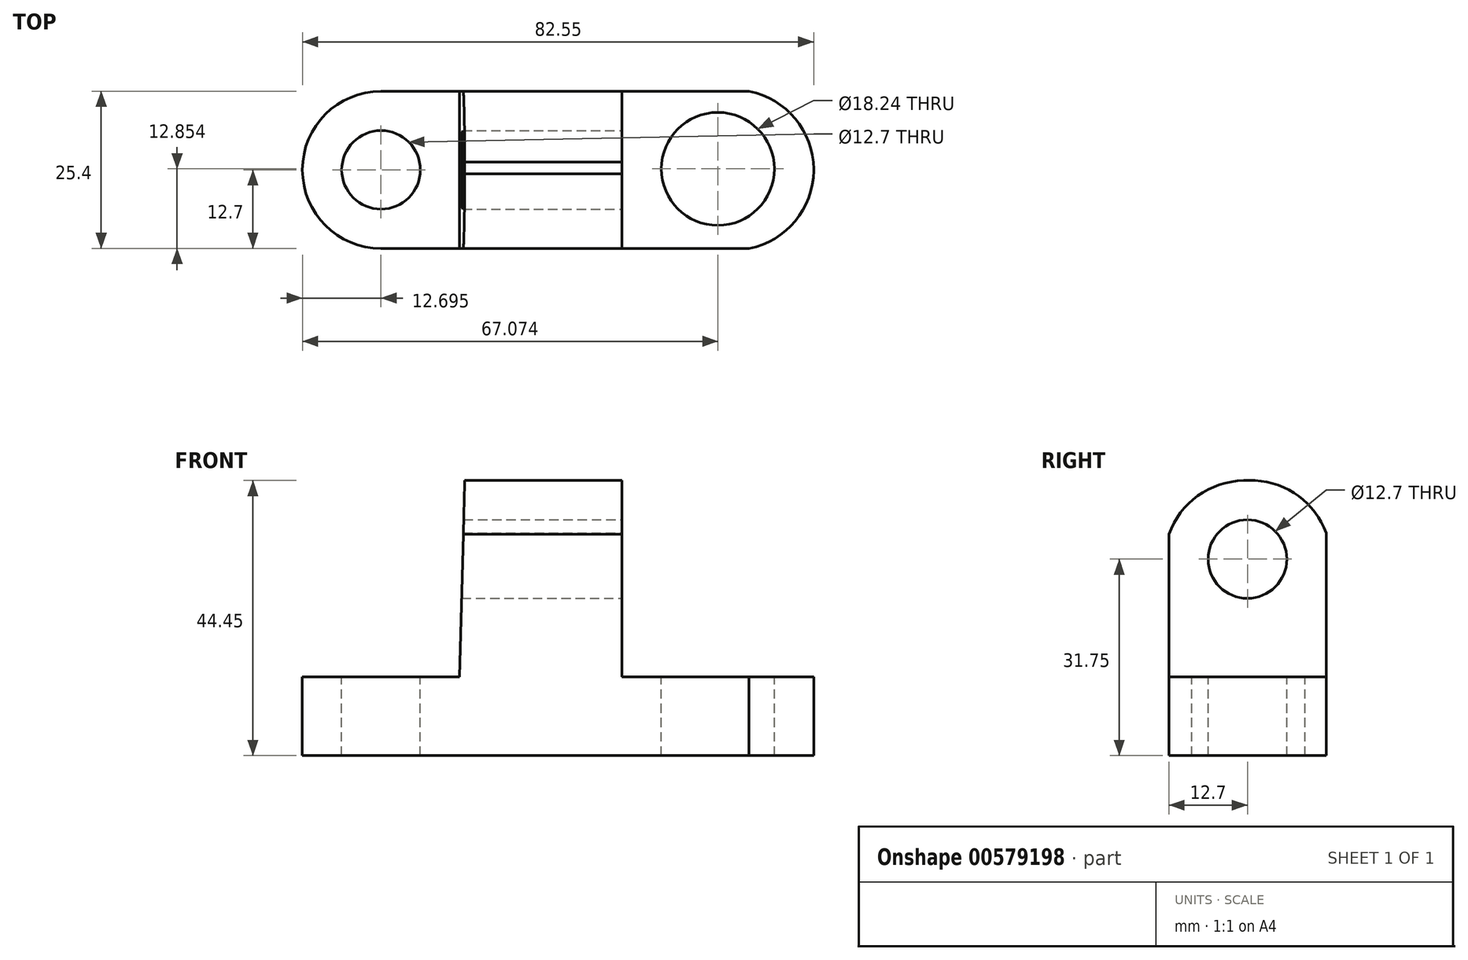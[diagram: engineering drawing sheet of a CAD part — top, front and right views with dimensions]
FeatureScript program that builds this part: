
annotation { "Feature Type Name" : "Feature", "Feature Type Description" : "" }
export const myFeature = defineFeature(function(context is Context, id is Id, definition is map)
    precondition{}
    {
        {
            var Q0;
            Q0=qCreatedBy(makeId("Front.planeOp"),FACE);
            var sketch = newSketch(context, id + "F0", { "sketchPlane" : qUnion([Q0])});
            skLineSegment(sketch, "E0", {"start": v(-96.25, 12.7) * mm, "end": v(-96.25, 0) * mm});
            skLineSegment(sketch, "E1", {"start": v(-96.25, 0) * mm, "end": v(-13.7, 0) * mm});
            skLineSegment(sketch, "E2", {"start": v(-13.7, 0) * mm, "end": v(-13.7, 12.7) * mm});
            skLineSegment(sketch, "E3", {"start": v(-13.7, 12.7) * mm, "end": v(-44.65, 12.7) * mm});
            skLineSegment(sketch, "E4", {"start": v(-44.65, 12.7) * mm, "end": v(-44.65, 44.45) * mm});
            skLineSegment(sketch, "E5", {"start": v(-44.65, 44.45) * mm, "end": v(-70.05, 44.45) * mm});
            skLineSegment(sketch, "E6", {"start": v(-96.25, 12.7) * mm, "end": v(-70.85, 12.7) * mm});
            skLineSegment(sketch, "E7", {"start": v(-70.85, 12.7) * mm, "end": v(-70.05, 44.45) * mm});
            skSolve(sketch);
        }
        {
            var Q0;
            Q0=makeQuery(id+"F0.imprint","IMPRINT",FACE,{"disambiguationData":[TD([[makeQuery(id+"F0.imprint","IMPRINT",EDGE,{"derivedFrom":sQuery(id+"F0.wireOp",EDGE,"E0")}),1.0]])]});
            extrude(context, id + "F1", {"entities" : qUnion([Q0]), "depth" : 25.4 * mm, "offsetDistance" : 25.4 * mm});
        }
        {
            var Q0;
            Q0=makeQuery(id+"F1.opExtrude","SWEPT_FACE",FACE,{"disambiguationData":[OSD([sQuery(id+"F0.wireOp",EDGE,"E4")])]});
            var sketch = newSketch(context, id + "F2", { "sketchPlane" : qUnion([Q0])});
            skCircle(sketch, "E8", {"center": v(-12.7, 31.75) * mm, "radius": 6.35 * mm});
            skSolve(sketch);
        }
        {
            var Q0;
            Q0=makeQuery(id+"F2.imprint","IMPRINT",FACE,{"disambiguationData":[TD([[makeQuery(id+"F2.imprint","IMPRINT",EDGE,{"derivedFrom":sQuery(id+"F2.wireOp",EDGE,"E8")}),1.0]])]});
            extrude(context, id + "F3", {"entities" : qUnion([Q0]), "operationType" : NewBodyOperationType.REMOVE, "endBound" : BoundingType.THROUGH_ALL, "oppositeDirection" : true, "depth" : 25.4 * mm, "offsetDistance" : 25.4 * mm});
        }
        {
            var Q0;
            Q0=makeQuery(id+"F1.opExtrude","SWEPT_FACE",FACE,{"disambiguationData":[OSD([sQuery(id+"F0.wireOp",EDGE,"E4")])]});
            var sketch = newSketch(context, id + "F4", { "sketchPlane" : qUnion([Q0])});
            skArc(sketch, "E9", {"start": v(-12.7, 44.45) * mm, "mid": v(-20.45, 42.15) * mm, "end": v(-25.4, 35.75) * mm});
            skArc(sketch, "E10", {"start": v(0, 35.95) * mm, "mid": v(-4.95, 42.3) * mm, "end": v(-12.7, 44.45) * mm});
            skSolve(sketch);
        }
        {
            var Q0;
            {var subQ0=sQuery(id+"F4.wireOp",EDGE,"E9");var subQ1=sQuery(id+"F0.wireOp",EDGE,"E4");var subQ2=makeQuery(id+"F1.opExtrude","CAP_EDGE",EDGE,{"disambiguationData":[OSD([subQ1])],"isStart":false});var subQ3=makeQuery(id+"F4.imprint","INTERSECT",VERTEX,{"derivedFrom":[subQ2,subQ0]});Q0=makeQuery(id+"F4.imprint","IMPRINT",FACE,{"disambiguationData":[TD([[makeQuery(id+"F4.imprint","IMPRINT",EDGE,{"disambiguationData":[TD([[subQ3,1.0]])],"derivedFrom":subQ0}),-1.0]])]});}
            var Q1;
            {var subQ0=sQuery(id+"F4.wireOp",EDGE,"E10");var subQ1=sQuery(id+"F0.wireOp",EDGE,"E4");var subQ2=makeQuery(id+"F1.opExtrude","CAP_EDGE",EDGE,{"disambiguationData":[OSD([subQ1])],"isStart":true});var subQ3=makeQuery(id+"F4.imprint","INTERSECT",VERTEX,{"derivedFrom":[subQ2,subQ0]});Q1=makeQuery(id+"F4.imprint","IMPRINT",FACE,{"disambiguationData":[TD([[makeQuery(id+"F4.imprint","IMPRINT",EDGE,{"disambiguationData":[TD([[subQ3,-1.0]])],"derivedFrom":subQ0}),-1.0]])]});}
            extrude(context, id + "F5", {"entities" : qUnion([Q0, Q1]), "operationType" : NewBodyOperationType.REMOVE, "endBound" : BoundingType.THROUGH_ALL, "oppositeDirection" : true, "depth" : 25.4 * mm, "offsetDistance" : 25.4 * mm});
        }
        {
            var Q0;
            Q0=makeQuery(id+"F1.opExtrude","SWEPT_FACE",FACE,{"disambiguationData":[OSD([sQuery(id+"F0.wireOp",EDGE,"E3")])]});
            var sketch = newSketch(context, id + "F6", { "sketchPlane" : qUnion([Q0])});
            skCircle(sketch, "E11", {"center": v(-29.18, -12.55) * mm, "radius": 9.12 * mm});
            skSolve(sketch);
        }
        {
            var Q0;
            Q0=makeQuery(id+"F6.imprint","IMPRINT",FACE,{"disambiguationData":[TD([[makeQuery(id+"F6.imprint","IMPRINT",EDGE,{"derivedFrom":sQuery(id+"F6.wireOp",EDGE,"E11")}),1.0]])]});
            extrude(context, id + "F7", {"entities" : qUnion([Q0]), "operationType" : NewBodyOperationType.REMOVE, "endBound" : BoundingType.THROUGH_ALL, "oppositeDirection" : true, "depth" : 25.4 * mm, "offsetDistance" : 25.4 * mm});
        }
        {
            var Q0;
            Q0=makeQuery(id+"F1.opExtrude","SWEPT_FACE",FACE,{"disambiguationData":[OSD([sQuery(id+"F0.wireOp",EDGE,"E6")])]});
            var sketch = newSketch(context, id + "F8", { "sketchPlane" : qUnion([Q0])});
            skCircle(sketch, "E12", {"center": v(-83.55, -12.7) * mm, "radius": 6.35 * mm});
            skSolve(sketch);
        }
        {
            var Q0;
            Q0=makeQuery(id+"F8.imprint","IMPRINT",FACE,{"disambiguationData":[TD([[makeQuery(id+"F8.imprint","IMPRINT",EDGE,{"derivedFrom":sQuery(id+"F8.wireOp",EDGE,"E12")}),1.0]])]});
            extrude(context, id + "F9", {"entities" : qUnion([Q0]), "operationType" : NewBodyOperationType.REMOVE, "endBound" : BoundingType.THROUGH_ALL, "oppositeDirection" : true, "depth" : 25.4 * mm, "offsetDistance" : 25.4 * mm});
        }
        {
            var Q0;
            Q0=makeQuery(id+"F1.opExtrude","SWEPT_FACE",FACE,{"disambiguationData":[OSD([sQuery(id+"F0.wireOp",EDGE,"E6")])]});
            var sketch = newSketch(context, id + "F10", { "sketchPlane" : qUnion([Q0])});
            skArc(sketch, "E13", {"start": v(-83.55, 0) * mm, "mid": v(-96.25, -12.7) * mm, "end": v(-83.55, -25.4) * mm});
            skSolve(sketch);
        }
        {
            var Q0;
            {var subQ0=sQuery(id+"F10.wireOp",EDGE,"E13");var subQ1=sQuery(id+"F0.wireOp",EDGE,"E6");var subQ2=makeQuery(id+"F1.opExtrude","CAP_EDGE",EDGE,{"disambiguationData":[OSD([subQ1])],"isStart":true});var subQ3=makeQuery(id+"F10.imprint","INTERSECT",VERTEX,{"derivedFrom":[subQ2,subQ0]});Q0=makeQuery(id+"F10.imprint","IMPRINT",FACE,{"disambiguationData":[TD([[makeQuery(id+"F10.imprint","IMPRINT",EDGE,{"disambiguationData":[TD([[subQ3,-1.0]])],"derivedFrom":subQ0}),-1.0]])]});}
            var Q1;
            {var subQ0=sQuery(id+"F10.wireOp",EDGE,"E13");var subQ1=sQuery(id+"F0.wireOp",EDGE,"E6");var subQ2=makeQuery(id+"F1.opExtrude","CAP_EDGE",EDGE,{"disambiguationData":[OSD([subQ1])],"isStart":false});var subQ3=makeQuery(id+"F10.imprint","INTERSECT",VERTEX,{"derivedFrom":[subQ2,subQ0]});Q1=makeQuery(id+"F10.imprint","IMPRINT",FACE,{"disambiguationData":[TD([[makeQuery(id+"F10.imprint","IMPRINT",EDGE,{"disambiguationData":[TD([[subQ3,1.0]])],"derivedFrom":subQ0}),-1.0]])]});}
            extrude(context, id + "F11", {"entities" : qUnion([Q0, Q1]), "operationType" : NewBodyOperationType.REMOVE, "endBound" : BoundingType.THROUGH_ALL, "oppositeDirection" : true, "depth" : 25.4 * mm, "offsetDistance" : 25.4 * mm});
        }
        {
            var Q0;
            Q0=makeQuery(id+"F1.opExtrude","SWEPT_FACE",FACE,{"disambiguationData":[OSD([sQuery(id+"F0.wireOp",EDGE,"E3")])]});
            var sketch = newSketch(context, id + "F12", { "sketchPlane" : qUnion([Q0])});
            skArc(sketch, "E14", {"start": v(-29.18, -25.4) * mm, "mid": v(-13.7, -12.7) * mm, "end": v(-29.18, 0) * mm});
            skSolve(sketch);
        }
        {
            var Q0;
            {var subQ0=sQuery(id+"F12.wireOp",EDGE,"E14");var subQ1=sQuery(id+"F0.wireOp",EDGE,"E3");var subQ4=makeQuery(id+"F1.opExtrude","CAP_EDGE",EDGE,{"disambiguationData":[OSD([subQ1])],"isStart":true});var subQ5=makeQuery(id+"F12.imprint","INTERSECT",VERTEX,{"disambiguationData":[OD(1.0)],"derivedFrom":[subQ4,subQ0]});Q0=makeQuery(id+"F12.imprint","IMPRINT",FACE,{"disambiguationData":[TD([[makeQuery(id+"F12.imprint","IMPRINT",EDGE,{"disambiguationData":[TD([[subQ5,1.0]])],"derivedFrom":subQ0}),-1.0]])]});}
            var Q1;
            {var subQ0=sQuery(id+"F12.wireOp",EDGE,"E14");var subQ1=sQuery(id+"F0.wireOp",EDGE,"E3");var subQ2=makeQuery(id+"F1.opExtrude","CAP_EDGE",EDGE,{"disambiguationData":[OSD([subQ1])],"isStart":false});var subQ3=makeQuery(id+"F12.imprint","INTERSECT",VERTEX,{"disambiguationData":[OD(1.0)],"derivedFrom":[subQ2,subQ0]});Q1=makeQuery(id+"F12.imprint","IMPRINT",FACE,{"disambiguationData":[TD([[makeQuery(id+"F12.imprint","IMPRINT",EDGE,{"disambiguationData":[TD([[subQ3,-1.0]])],"derivedFrom":subQ0}),-1.0]])]});}
            extrude(context, id + "F13", {"entities" : qUnion([Q0, Q1]), "operationType" : NewBodyOperationType.REMOVE, "endBound" : BoundingType.THROUGH_ALL, "oppositeDirection" : true, "depth" : 25.4 * mm, "offsetDistance" : 25.4 * mm});
        }
    });
